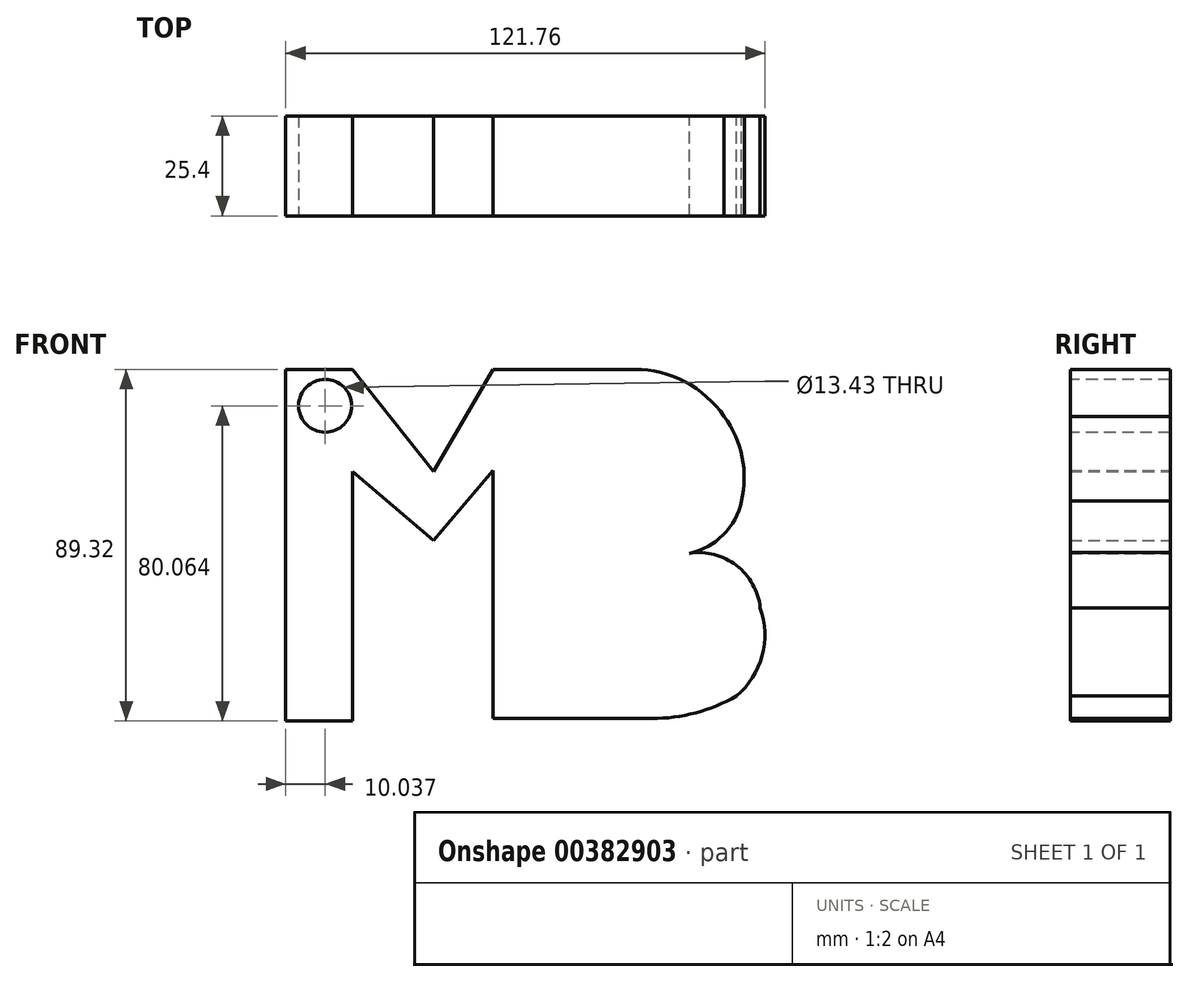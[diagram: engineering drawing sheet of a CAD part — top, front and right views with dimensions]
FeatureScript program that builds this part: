
annotation { "Feature Type Name" : "Feature", "Feature Type Description" : "" }
export const myFeature = defineFeature(function(context is Context, id is Id, definition is map)
    precondition{}
    {
        {
            var Q0;
            Q0=qCreatedBy(makeId("Front.planeOp"),FACE);
            var sketch = newSketch(context, id + "F0", { "sketchPlane" : qUnion([Q0])});
            skLineSegment(sketch, "E0", {"start": v(-52.7, 43.4) * mm, "end": v(-52.7, -45.92) * mm});
            skLineSegment(sketch, "E1", {"start": v(-52.7, 43.4) * mm, "end": v(-35.67, 43.4) * mm});
            skLineSegment(sketch, "E2", {"start": v(-35.67, 43.4) * mm, "end": v(-15.15, 17.52) * mm});
            skLineSegment(sketch, "E3", {"start": v(-15.15, 17.52) * mm, "end": v(0, 43.4) * mm});
            skLineSegment(sketch, "E4", {"start": v(-52.7, -45.92) * mm, "end": v(-35.67, -45.92) * mm});
            skLineSegment(sketch, "E5", {"start": v(-35.67, -45.92) * mm, "end": v(-35.67, 17.52) * mm});
            skLineSegment(sketch, "E6", {"start": v(-35.67, 17.52) * mm, "end": v(-15.15, 0) * mm});
            skLineSegment(sketch, "E7", {"start": v(-15.15, 0) * mm, "end": v(0, 17.74) * mm});
            skLineSegment(sketch, "E8", {"start": v(0, 17.74) * mm, "end": v(0, -45.3) * mm});
            skLineSegment(sketch, "E9", {"start": v(0, 43.4) * mm, "end": v(35.98, 43.4) * mm});
            skLineSegment(sketch, "E10", {"start": v(0, -45.3) * mm, "end": v(40.4, -45.3) * mm});
            skArc(sketch, "E11", {"start": v(58.7, 31.4) * mm, "mid": v(48.83, 40.22) * mm, "end": v(35.98, 43.4) * mm});
            skArc(sketch, "E12", {"start": v(63.12, 9.94) * mm, "mid": v(63.26, 21.16) * mm, "end": v(58.7, 31.4) * mm});
            skArc(sketch, "E13", {"start": v(49.87, -3.31) * mm, "mid": v(58.46, 1.35) * mm, "end": v(63.12, 9.94) * mm});
            skArc(sketch, "E14", {"start": v(67.86, -17.2) * mm, "mid": v(61.84, -6.4) * mm, "end": v(49.87, -3.31) * mm});
            skArc(sketch, "E15", {"start": v(61.84, -39.61) * mm, "mid": v(68.35, -29.35) * mm, "end": v(67.86, -17.2) * mm});
            skPoint(sketch, "E15.startSnap0", {"position": v(61.84, -6.4) * mm});
            skArc(sketch, "E16", {"start": v(40.4, -45.3) * mm, "mid": v(51.49, -43.85) * mm, "end": v(61.84, -39.61) * mm});
            skSolve(sketch);
        }
        {
            var Q0;
            Q0=makeQuery(id+"F0.imprint","IMPRINT",FACE,{"disambiguationData":[TD([[makeQuery(id+"F0.imprint","IMPRINT",EDGE,{"derivedFrom":sQuery(id+"F0.wireOp",EDGE,"E0")}),1.0]])]});
            extrude(context, id + "F1", {"entities" : qUnion([Q0]), "depth" : 25.4 * mm});
        }
        {
            var Q0;
            Q0=makeQuery(id+"F1.opExtrude","CAP_FACE",FACE,{"disambiguationData":[OSD([sQuery(id+"F0.wireOp",EDGE,"E0"),sQuery(id+"F0.wireOp",EDGE,"E1"),sQuery(id+"F0.wireOp",EDGE,"E2"),sQuery(id+"F0.wireOp",EDGE,"E3"),sQuery(id+"F0.wireOp",EDGE,"E4"),sQuery(id+"F0.wireOp",EDGE,"E5"),sQuery(id+"F0.wireOp",EDGE,"E6"),sQuery(id+"F0.wireOp",EDGE,"E7"),sQuery(id+"F0.wireOp",EDGE,"E8"),sQuery(id+"F0.wireOp",EDGE,"E9"),sQuery(id+"F0.wireOp",EDGE,"E10"),sQuery(id+"F0.wireOp",EDGE,"E11"),sQuery(id+"F0.wireOp",EDGE,"E12"),sQuery(id+"F0.wireOp",EDGE,"E13"),sQuery(id+"F0.wireOp",EDGE,"E14"),sQuery(id+"F0.wireOp",EDGE,"E15"),sQuery(id+"F0.wireOp",EDGE,"E16")])],"isStart":false});
            var sketch = newSketch(context, id + "F2", { "sketchPlane" : qUnion([Q0])});
            skCircle(sketch, "E17", {"center": v(-42.67, 34.14) * mm, "radius": 6.72 * mm});
            skSolve(sketch);
        }
        {
            var Q0;
            Q0=makeQuery(id+"F2.imprint","IMPRINT",FACE,{"disambiguationData":[TD([[makeQuery(id+"F2.imprint","IMPRINT",EDGE,{"derivedFrom":sQuery(id+"F2.wireOp",EDGE,"E17")}),1.0]])]});
            extrude(context, id + "F3", {"entities" : qUnion([Q0]), "operationType" : NewBodyOperationType.REMOVE, "oppositeDirection" : true, "depth" : 127 * mm});
        }
    });
